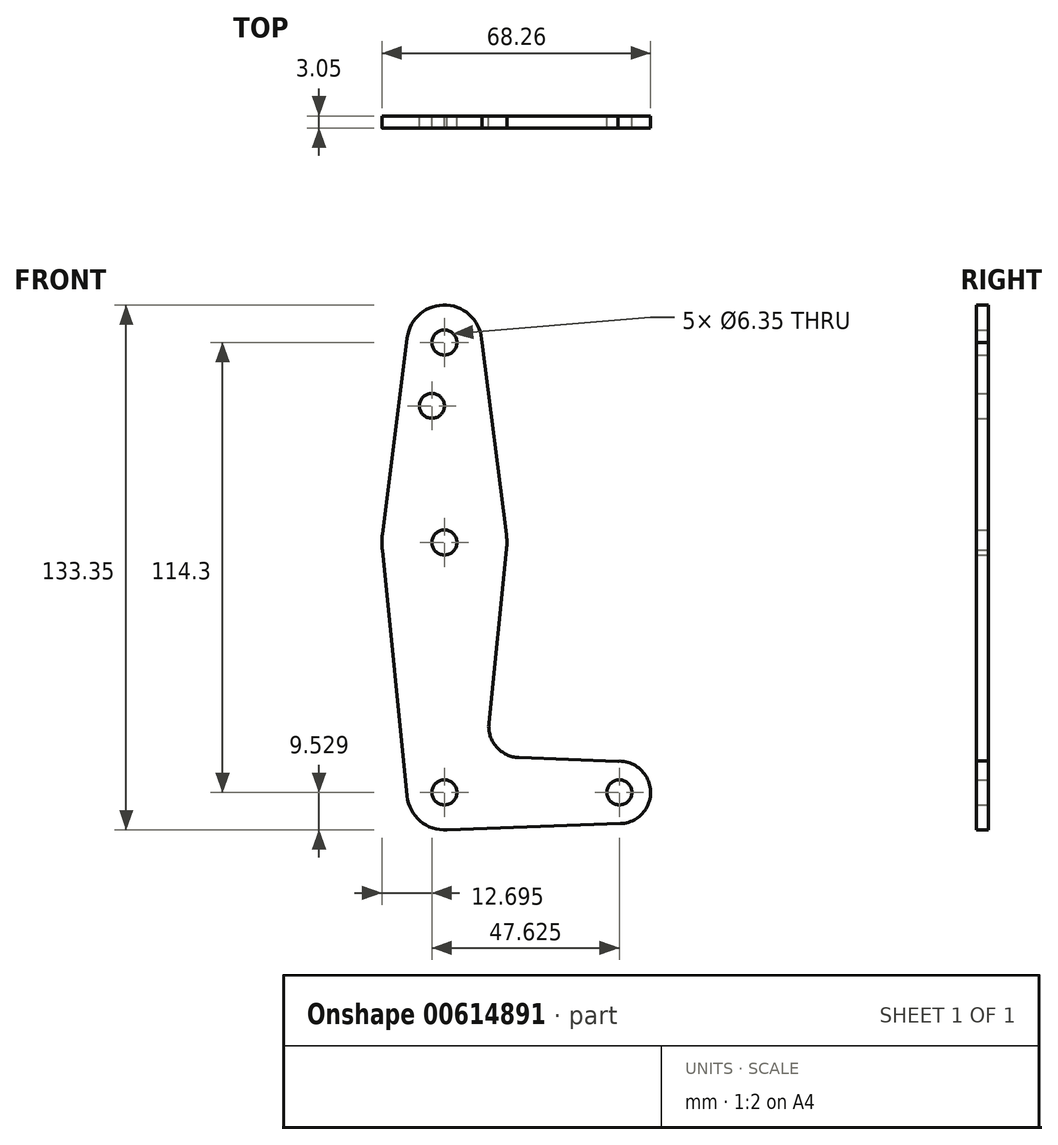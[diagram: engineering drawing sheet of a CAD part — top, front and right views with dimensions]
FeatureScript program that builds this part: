
annotation { "Feature Type Name" : "Feature", "Feature Type Description" : "" }
export const myFeature = defineFeature(function(context is Context, id is Id, definition is map)
    precondition{}
    {
        {
            var Q0;
            Q0=qCreatedBy(makeId("Front.planeOp"),FACE);
            var sketch = newSketch(context, id + "F0", { "sketchPlane" : qUnion([Q0])});
            skLineSegment(sketch, "E0", {"start": v(0, 100.2) * mm, "end": v(0, 49.4) * mm, "construction": true});
            skLineSegment(sketch, "E1", {"start": v(0, 49.4) * mm, "end": v(0, -14.1) * mm, "construction": true});
            skLineSegment(sketch, "E2", {"start": v(0, -14.1) * mm, "end": v(44.45, -14.1) * mm, "construction": true});
            skCircle(sketch, "E3", {"center": v(0, 100.2) * mm, "radius": 9.53 * mm});
            skCircle(sketch, "E4", {"center": v(0, 49.4) * mm, "radius": 15.88 * mm});
            skCircle(sketch, "E5", {"center": v(0, -14.1) * mm, "radius": 9.53 * mm});
            skCircle(sketch, "E6", {"center": v(44.45, -14.1) * mm, "radius": 7.94 * mm});
            skLineSegment(sketch, "E7", {"start": v(-9.45, 101.39) * mm, "end": v(-15.75, 51.38) * mm});
            skLineSegment(sketch, "E8", {"start": v(-15.82, 48.08) * mm, "end": v(-9.48, -15.05) * mm});
            skPoint(sketch, "E9.orphan", {"position": v(9.52, 100.2) * mm});
            skLineSegment(sketch, "E10", {"start": v(9.52, 100.2) * mm, "end": v(15.75, 51.4) * mm});
            skLineSegment(sketch, "E11", {"start": v(11.3, 3.49) * mm, "end": v(15.8, 47.8) * mm});
            skLineSegment(sketch, "E12", {"start": v(0, -23.63) * mm, "end": v(44.73, -22.03) * mm});
            skLineSegment(sketch, "E13", {"start": v(44.06, -6.17) * mm, "end": v(18.93, -5.26) * mm});
            skCircle(sketch, "E14", {"center": v(-3.17, 84.11) * mm, "radius": 3.18 * mm});
            skCircle(sketch, "E15", {"center": v(0, 100.2) * mm, "radius": 3.18 * mm});
            skCircle(sketch, "E16", {"center": v(0, 49.4) * mm, "radius": 3.18 * mm});
            skCircle(sketch, "E17", {"center": v(0, -14.1) * mm, "radius": 3.18 * mm});
            skCircle(sketch, "E18", {"center": v(44.45, -14.1) * mm, "radius": 3.18 * mm});
            skArc(sketch, "E19.filletArc", {"start": v(11.3, 3.49) * mm, "mid": v(13.22, -2.54) * mm, "end": v(18.93, -5.26) * mm});
            skSolve(sketch);
        }
        {
            var Q0;
            Q0 = qSketchRegion(id + "F0", true);
            extrude(context, id + "F1", {"entities" : qUnion([Q0]), "depth" : 3.05 * mm, "offsetDistance" : 25.4 * mm});
        }
    });
